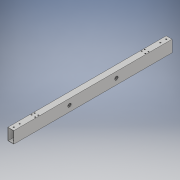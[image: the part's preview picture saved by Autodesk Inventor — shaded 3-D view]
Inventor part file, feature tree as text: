
AUTODESK INVENTOR PART (.ipt)
format: ipt  version: 2018 (Build 220112000, 112)  size: 164,864 bytes
history: native  units: in
note: dims shown in document units (in); Inventor stores cm internally (conversion verified against a paired STEP export)
features: extrude x4, sketch x4
ambient origin geometry x8: Origin, YZ Plane, XZ Plane, XY Plane, X Axis, Y Axis, Z Axis, Center Point
bodies: Solid1 (feature_tree)
feature tree (8):
  extrude  "Extrusion1"  Depth=2.0in
  extrude  "Extrusion2"  Depth=27.0in TaperAngle=0.0deg
  extrude  "Extrusion9"  Depth=1.0in
  extrude  "Extrusion10"  Depth=1.0in TaperAngle=0.0deg
  sketch  "Sketch1"  dims[d0=1.0in d1=2.0in]
  sketch  "Sketch2"  dims[d2=0.0625in d3=27.0in d4=0.0in]
  sketch  "Sketch6"  dims[d5=0.5in d6=1.0in]
  sketch  "Sketch7"  dims[d7=0.2031in d8=6.5in d9=0.0in d32=9.5in d33=0.59in d34=1.0in d35=0.0in d37=4.625in d38=0.25in d39=0.187in d40=0.6299in d41=0.5315in d42=0.1811in d43=3.9375in d44=0.0in d45=0.1811in d46=0.1811in d47=0.1811in]
